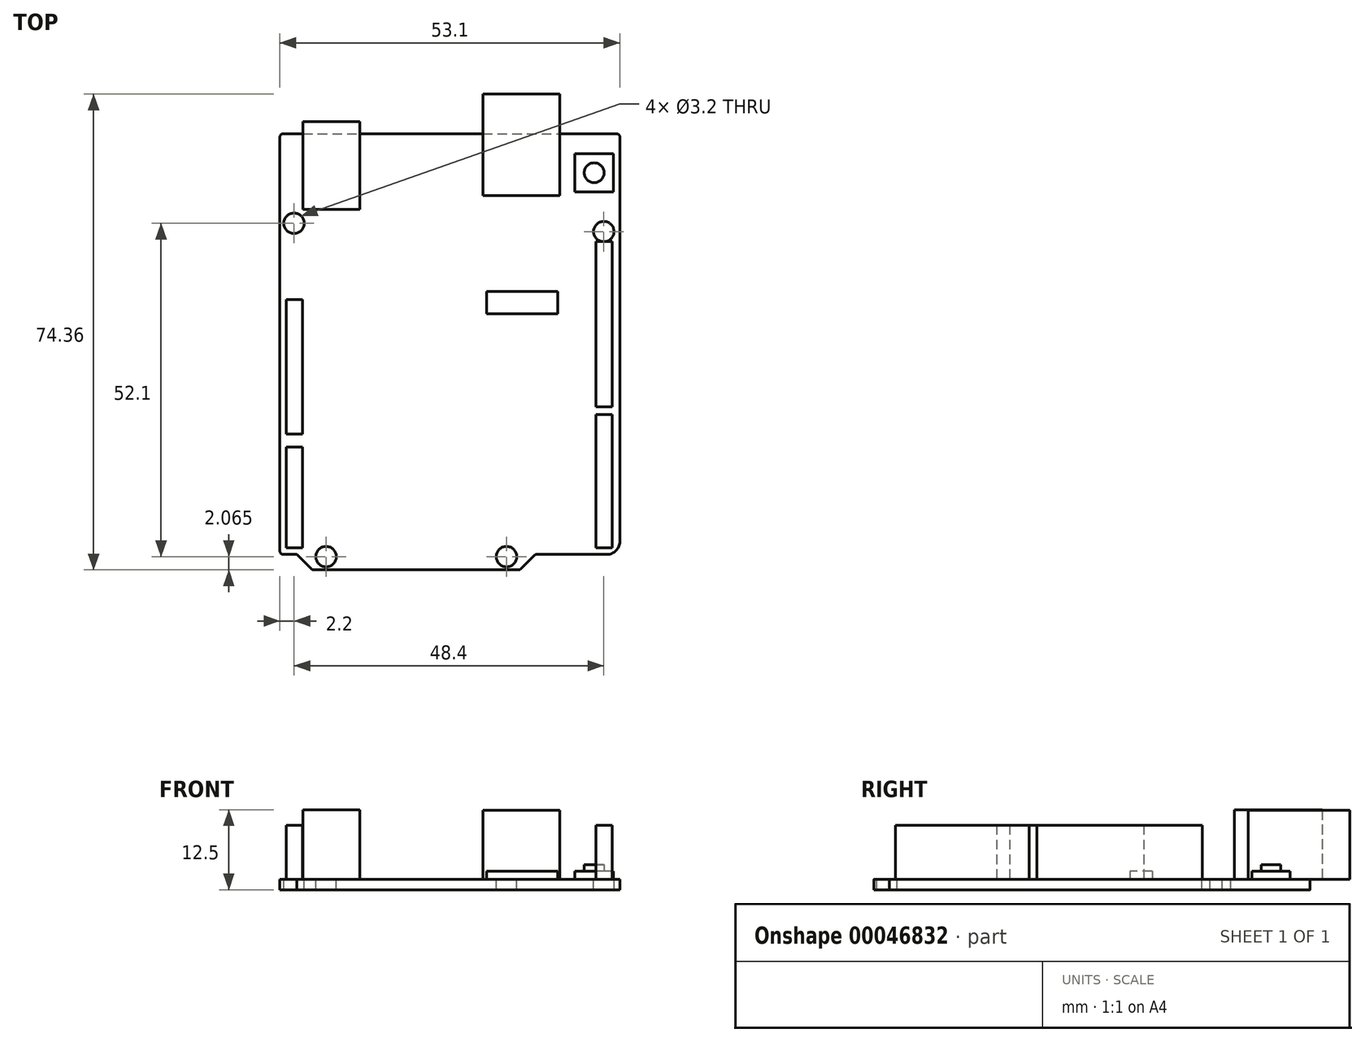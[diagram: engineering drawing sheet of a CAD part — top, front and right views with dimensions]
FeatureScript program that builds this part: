
annotation { "Feature Type Name" : "Feature", "Feature Type Description" : "" }
export const myFeature = defineFeature(function(context is Context, id is Id, definition is map)
    precondition{}
    {
        {
            var Q0;
            Q0=qCreatedBy(makeId("Top.planeOp"),FACE);
            var sketch = newSketch(context, id + "F0", { "sketchPlane" : qUnion([Q0])});
            skLineSegment(sketch, "E0", {"start": v(-26.05, 32.87) * mm, "end": v(26.05, 32.88) * mm});
            skLineSegment(sketch, "E1", {"start": v(26.55, 32.38) * mm, "end": v(26.55, -30.87) * mm});
            skLineSegment(sketch, "E2", {"start": v(24.55, -32.87) * mm, "end": v(13.56, -32.87) * mm});
            skLineSegment(sketch, "E3", {"start": v(13.2, -33.02) * mm, "end": v(11.09, -35.14) * mm});
            skLineSegment(sketch, "E4", {"start": v(10.73, -35.28) * mm, "end": v(-21.28, -35.29) * mm});
            skLineSegment(sketch, "E5", {"start": v(-21.64, -35.14) * mm, "end": v(-23.9, -32.88) * mm});
            skLineSegment(sketch, "E6", {"start": v(-23.9, -32.88) * mm, "end": v(-26.05, -32.88) * mm});
            skLineSegment(sketch, "E7", {"start": v(-26.55, -32.38) * mm, "end": v(-26.55, 32.37) * mm});
            skPoint(sketch, "E8.visualSharp", {"position": v(-26.55, 32.87) * mm});
            skArc(sketch, "E8.filletArc", {"start": v(-26.05, 32.87) * mm, "mid": v(-26.4, 32.73) * mm, "end": v(-26.55, 32.37) * mm});
            skPoint(sketch, "E9.visualSharp", {"position": v(26.55, 32.88) * mm});
            skArc(sketch, "E9.filletArc", {"start": v(26.55, 32.38) * mm, "mid": v(26.4, 32.73) * mm, "end": v(26.05, 32.88) * mm});
            skPoint(sketch, "E10.visualSharp", {"position": v(-26.55, -32.88) * mm});
            skArc(sketch, "E10.filletArc", {"start": v(-26.55, -32.38) * mm, "mid": v(-26.4, -32.73) * mm, "end": v(-26.05, -32.88) * mm});
            skPoint(sketch, "E11.visualSharp", {"position": v(-21.49, -35.29) * mm});
            skArc(sketch, "E11.filletArc", {"start": v(-21.64, -35.14) * mm, "mid": v(-21.47, -35.25) * mm, "end": v(-21.28, -35.28) * mm});
            skPoint(sketch, "E12.visualSharp", {"position": v(10.94, -35.28) * mm});
            skArc(sketch, "E12.filletArc", {"start": v(10.73, -35.28) * mm, "mid": v(10.92, -35.25) * mm, "end": v(11.09, -35.14) * mm});
            skPoint(sketch, "E13.visualSharp", {"position": v(13.35, -32.87) * mm});
            skArc(sketch, "E13.filletArc", {"start": v(13.56, -32.87) * mm, "mid": v(13.37, -32.91) * mm, "end": v(13.2, -33.02) * mm});
            skPoint(sketch, "E14.visualSharp", {"position": v(26.55, -32.87) * mm});
            skArc(sketch, "E14.filletArc", {"start": v(24.55, -32.87) * mm, "mid": v(25.96, -32.29) * mm, "end": v(26.55, -30.87) * mm});
            skSolve(sketch);
        }
        {
            var Q0;
            Q0 = qSketchRegion(id + "F0", true);
            extrude(context, id + "F1", {"entities" : qUnion([Q0]), "depth" : 1.6 * mm});
        }
        {
            var Q0;
            Q0=makeQuery(id+"F1.opExtrude","CAP_FACE",FACE,{"disambiguationData":[OSD([sQuery(id+"F0.wireOp",EDGE,"E0"),sQuery(id+"F0.wireOp",EDGE,"E1"),sQuery(id+"F0.wireOp",EDGE,"E2"),sQuery(id+"F0.wireOp",EDGE,"E3"),sQuery(id+"F0.wireOp",EDGE,"E4"),sQuery(id+"F0.wireOp",EDGE,"E5"),sQuery(id+"F0.wireOp",EDGE,"E6"),sQuery(id+"F0.wireOp",EDGE,"E7"),sQuery(id+"F0.wireOp",EDGE,"E8.filletArc"),sQuery(id+"F0.wireOp",EDGE,"E9.filletArc"),sQuery(id+"F0.wireOp",EDGE,"E10.filletArc"),sQuery(id+"F0.wireOp",EDGE,"E11.filletArc"),sQuery(id+"F0.wireOp",EDGE,"E12.filletArc"),sQuery(id+"F0.wireOp",EDGE,"E13.filletArc"),sQuery(id+"F0.wireOp",EDGE,"E14.filletArc")])],"isStart":false});
            var sketch = newSketch(context, id + "F2", { "sketchPlane" : qUnion([Q0])});
            skLineSegment(sketch, "E15.bottom", {"start": v(17.15, 39.08) * mm, "end": v(5.15, 39.08) * mm});
            skLineSegment(sketch, "E15.top", {"start": v(17.15, 23.2) * mm, "end": v(5.15, 23.2) * mm});
            skLineSegment(sketch, "E15.left", {"start": v(17.15, 39.08) * mm, "end": v(17.15, 23.2) * mm});
            skLineSegment(sketch, "E15.right", {"start": v(5.15, 39.08) * mm, "end": v(5.15, 23.2) * mm});
            skSolve(sketch);
        }
        {
            var Q0;
            Q0 = qSketchRegion(id + "F2", true);
            extrude(context, id + "F3", {"entities" : qUnion([Q0]), "depth" : 10.82 * mm});
        }
        {
            var Q0;
            Q0=makeQuery(id+"F1.opExtrude","CAP_FACE",FACE,{"disambiguationData":[OSD([sQuery(id+"F0.wireOp",EDGE,"E0"),sQuery(id+"F0.wireOp",EDGE,"E1"),sQuery(id+"F0.wireOp",EDGE,"E2"),sQuery(id+"F0.wireOp",EDGE,"E3"),sQuery(id+"F0.wireOp",EDGE,"E4"),sQuery(id+"F0.wireOp",EDGE,"E5"),sQuery(id+"F0.wireOp",EDGE,"E6"),sQuery(id+"F0.wireOp",EDGE,"E7"),sQuery(id+"F0.wireOp",EDGE,"E8.filletArc"),sQuery(id+"F0.wireOp",EDGE,"E9.filletArc"),sQuery(id+"F0.wireOp",EDGE,"E10.filletArc"),sQuery(id+"F0.wireOp",EDGE,"E11.filletArc"),sQuery(id+"F0.wireOp",EDGE,"E12.filletArc"),sQuery(id+"F0.wireOp",EDGE,"E13.filletArc"),sQuery(id+"F0.wireOp",EDGE,"E14.filletArc")])],"isStart":false});
            var sketch = newSketch(context, id + "F4", { "sketchPlane" : qUnion([Q0])});
            skLineSegment(sketch, "E16.bottom", {"start": v(-14.05, 34.77) * mm, "end": v(-22.95, 34.77) * mm});
            skLineSegment(sketch, "E16.top", {"start": v(-14.05, 21.07) * mm, "end": v(-22.95, 21.07) * mm});
            skLineSegment(sketch, "E16.left", {"start": v(-14.05, 34.77) * mm, "end": v(-14.05, 21.07) * mm});
            skLineSegment(sketch, "E16.right", {"start": v(-22.95, 34.77) * mm, "end": v(-22.95, 21.07) * mm});
            skSolve(sketch);
        }
        {
            var Q0;
            Q0 = qSketchRegion(id + "F4", true);
            extrude(context, id + "F5", {"entities" : qUnion([Q0]), "depth" : 10.9 * mm});
        }
        {
            var Q0;
            Q0=makeQuery(id+"F1.opExtrude","CAP_FACE",FACE,{"disambiguationData":[OSD([sQuery(id+"F0.wireOp",EDGE,"E0"),sQuery(id+"F0.wireOp",EDGE,"E1"),sQuery(id+"F0.wireOp",EDGE,"E2"),sQuery(id+"F0.wireOp",EDGE,"E3"),sQuery(id+"F0.wireOp",EDGE,"E4"),sQuery(id+"F0.wireOp",EDGE,"E5"),sQuery(id+"F0.wireOp",EDGE,"E6"),sQuery(id+"F0.wireOp",EDGE,"E7"),sQuery(id+"F0.wireOp",EDGE,"E8.filletArc"),sQuery(id+"F0.wireOp",EDGE,"E9.filletArc"),sQuery(id+"F0.wireOp",EDGE,"E10.filletArc"),sQuery(id+"F0.wireOp",EDGE,"E11.filletArc"),sQuery(id+"F0.wireOp",EDGE,"E12.filletArc"),sQuery(id+"F0.wireOp",EDGE,"E13.filletArc"),sQuery(id+"F0.wireOp",EDGE,"E14.filletArc")])],"isStart":false});
            var sketch = newSketch(context, id + "F6", { "sketchPlane" : qUnion([Q0])});
            skCircle(sketch, "E17", {"center": v(-19.35, -33.23) * mm, "radius": 1.6 * mm});
            skCircle(sketch, "E18", {"center": v(8.85, -33.22) * mm, "radius": 1.6 * mm});
            skCircle(sketch, "E19", {"center": v(24.05, 17.57) * mm, "radius": 1.6 * mm});
            skCircle(sketch, "E20", {"center": v(-24.35, 18.87) * mm, "radius": 1.6 * mm});
            skSolve(sketch);
        }
        {
            var Q0;
            Q0 = qSketchRegion(id + "F6", true);
            extrude(context, id + "F7", {"entities" : qUnion([Q0]), "operationType" : NewBodyOperationType.REMOVE, "oppositeDirection" : true, "depth" : 3 * mm});
        }
        {
            var Q0;
            Q0=makeQuery(id+"F1.opExtrude","CAP_FACE",FACE,{"disambiguationData":[OSD([sQuery(id+"F0.wireOp",EDGE,"E0"),sQuery(id+"F0.wireOp",EDGE,"E1"),sQuery(id+"F0.wireOp",EDGE,"E2"),sQuery(id+"F0.wireOp",EDGE,"E3"),sQuery(id+"F0.wireOp",EDGE,"E4"),sQuery(id+"F0.wireOp",EDGE,"E5"),sQuery(id+"F0.wireOp",EDGE,"E6"),sQuery(id+"F0.wireOp",EDGE,"E7"),sQuery(id+"F0.wireOp",EDGE,"E8.filletArc"),sQuery(id+"F0.wireOp",EDGE,"E9.filletArc"),sQuery(id+"F0.wireOp",EDGE,"E10.filletArc"),sQuery(id+"F0.wireOp",EDGE,"E11.filletArc"),sQuery(id+"F0.wireOp",EDGE,"E12.filletArc"),sQuery(id+"F0.wireOp",EDGE,"E13.filletArc"),sQuery(id+"F0.wireOp",EDGE,"E14.filletArc")])],"isStart":false});
            var sketch = newSketch(context, id + "F8", { "sketchPlane" : qUnion([Q0])});
            skLineSegment(sketch, "E21.bottom", {"start": v(25.35, 16.03) * mm, "end": v(22.85, 16.03) * mm});
            skLineSegment(sketch, "E21.top", {"start": v(25.35, -9.82) * mm, "end": v(22.85, -9.82) * mm});
            skLineSegment(sketch, "E21.left", {"start": v(25.35, 16.03) * mm, "end": v(25.35, -9.82) * mm});
            skLineSegment(sketch, "E21.right", {"start": v(22.85, 16.03) * mm, "end": v(22.85, -9.82) * mm});
            skLineSegment(sketch, "E22.bottom", {"start": v(25.35, -11.02) * mm, "end": v(22.85, -11.02) * mm});
            skLineSegment(sketch, "E22.top", {"start": v(25.35, -31.87) * mm, "end": v(22.85, -31.87) * mm});
            skLineSegment(sketch, "E22.left", {"start": v(25.35, -11.02) * mm, "end": v(25.35, -31.87) * mm});
            skLineSegment(sketch, "E22.right", {"start": v(22.85, -11.02) * mm, "end": v(22.85, -31.87) * mm});
            skLineSegment(sketch, "E23.bottom", {"start": v(-23.05, 6.92) * mm, "end": v(-25.55, 6.92) * mm});
            skLineSegment(sketch, "E23.top", {"start": v(-23.05, -14.08) * mm, "end": v(-25.55, -14.08) * mm});
            skLineSegment(sketch, "E23.left", {"start": v(-23.05, 6.92) * mm, "end": v(-23.05, -14.08) * mm});
            skLineSegment(sketch, "E23.right", {"start": v(-25.55, 6.92) * mm, "end": v(-25.55, -14.08) * mm});
            skLineSegment(sketch, "E24.bottom", {"start": v(-23.05, -16.08) * mm, "end": v(-25.55, -16.08) * mm});
            skLineSegment(sketch, "E24.top", {"start": v(-23.05, -31.88) * mm, "end": v(-25.55, -31.88) * mm});
            skLineSegment(sketch, "E24.left", {"start": v(-23.05, -16.08) * mm, "end": v(-23.05, -31.88) * mm});
            skLineSegment(sketch, "E24.right", {"start": v(-25.55, -16.08) * mm, "end": v(-25.55, -31.88) * mm});
            skSolve(sketch);
        }
        {
            var Q0;
            Q0 = qSketchRegion(id + "F8", true);
            extrude(context, id + "F9", {"entities" : qUnion([Q0]), "depth" : 8.5 * mm});
        }
        {
            var Q0;
            Q0=makeQuery(id+"F1.opExtrude","CAP_FACE",FACE,{"disambiguationData":[OSD([sQuery(id+"F0.wireOp",EDGE,"E0"),sQuery(id+"F0.wireOp",EDGE,"E1"),sQuery(id+"F0.wireOp",EDGE,"E2"),sQuery(id+"F0.wireOp",EDGE,"E3"),sQuery(id+"F0.wireOp",EDGE,"E4"),sQuery(id+"F0.wireOp",EDGE,"E5"),sQuery(id+"F0.wireOp",EDGE,"E6"),sQuery(id+"F0.wireOp",EDGE,"E7"),sQuery(id+"F0.wireOp",EDGE,"E8.filletArc"),sQuery(id+"F0.wireOp",EDGE,"E9.filletArc"),sQuery(id+"F0.wireOp",EDGE,"E10.filletArc"),sQuery(id+"F0.wireOp",EDGE,"E11.filletArc"),sQuery(id+"F0.wireOp",EDGE,"E12.filletArc"),sQuery(id+"F0.wireOp",EDGE,"E13.filletArc"),sQuery(id+"F0.wireOp",EDGE,"E14.filletArc")])],"isStart":false});
            var sketch = newSketch(context, id + "F10", { "sketchPlane" : qUnion([Q0])});
            skLineSegment(sketch, "E25.bottom", {"start": v(25.55, 29.78) * mm, "end": v(19.55, 29.78) * mm});
            skLineSegment(sketch, "E25.top", {"start": v(25.55, 23.78) * mm, "end": v(19.55, 23.78) * mm});
            skLineSegment(sketch, "E25.left", {"start": v(25.55, 29.78) * mm, "end": v(25.55, 23.78) * mm});
            skLineSegment(sketch, "E25.right", {"start": v(19.55, 29.78) * mm, "end": v(19.55, 23.78) * mm});
            skSolve(sketch);
        }
        {
            var Q0;
            Q0 = qSketchRegion(id + "F10", true);
            extrude(context, id + "F11", {"entities" : qUnion([Q0]), "depth" : 1.3 * mm});
        }
        {
            var Q0;
            Q0=makeQuery(id+"F11.opExtrude","CAP_FACE",FACE,{"disambiguationData":[OSD([sQuery(id+"F10.wireOp",EDGE,"E25.bottom"),sQuery(id+"F10.wireOp",EDGE,"E25.top"),sQuery(id+"F10.wireOp",EDGE,"E25.left"),sQuery(id+"F10.wireOp",EDGE,"E25.right")])],"isStart":false});
            var sketch = newSketch(context, id + "F12", { "sketchPlane" : qUnion([Q0])});
            skCircle(sketch, "E26", {"center": v(22.55, 26.78) * mm, "radius": 1.55 * mm});
            skPoint(sketch, "E26.centerSnap0", {"position": v(22.55, 23.78) * mm});
            skSolve(sketch);
        }
        {
            var Q0;
            Q0 = qSketchRegion(id + "F12", true);
            extrude(context, id + "F13", {"entities" : qUnion([Q0]), "operationType" : NewBodyOperationType.ADD, "depth" : 1 * mm});
        }
        {
            var Q0;
            Q0=makeQuery(id+"F1.opExtrude","CAP_FACE",FACE,{"disambiguationData":[OSD([sQuery(id+"F0.wireOp",EDGE,"E0"),sQuery(id+"F0.wireOp",EDGE,"E1"),sQuery(id+"F0.wireOp",EDGE,"E2"),sQuery(id+"F0.wireOp",EDGE,"E3"),sQuery(id+"F0.wireOp",EDGE,"E4"),sQuery(id+"F0.wireOp",EDGE,"E5"),sQuery(id+"F0.wireOp",EDGE,"E6"),sQuery(id+"F0.wireOp",EDGE,"E7"),sQuery(id+"F0.wireOp",EDGE,"E8.filletArc"),sQuery(id+"F0.wireOp",EDGE,"E9.filletArc"),sQuery(id+"F0.wireOp",EDGE,"E10.filletArc"),sQuery(id+"F0.wireOp",EDGE,"E11.filletArc"),sQuery(id+"F0.wireOp",EDGE,"E12.filletArc"),sQuery(id+"F0.wireOp",EDGE,"E13.filletArc"),sQuery(id+"F0.wireOp",EDGE,"E14.filletArc")])],"isStart":false});
            var sketch = newSketch(context, id + "F14", { "sketchPlane" : qUnion([Q0])});
            skLineSegment(sketch, "E27.bottom", {"start": v(5.75, 8.22) * mm, "end": v(16.85, 8.22) * mm});
            skLineSegment(sketch, "E27.top", {"start": v(5.75, 4.72) * mm, "end": v(16.85, 4.72) * mm});
            skLineSegment(sketch, "E27.left", {"start": v(5.75, 8.22) * mm, "end": v(5.75, 4.72) * mm});
            skLineSegment(sketch, "E27.right", {"start": v(16.85, 8.22) * mm, "end": v(16.85, 4.72) * mm});
            skSolve(sketch);
        }
        {
            var Q0;
            Q0 = qSketchRegion(id + "F14", true);
            extrude(context, id + "F15", {"entities" : qUnion([Q0]), "depth" : 1.3 * mm});
        }
    });
